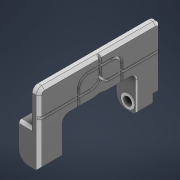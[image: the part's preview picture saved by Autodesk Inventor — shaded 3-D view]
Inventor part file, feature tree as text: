
AUTODESK INVENTOR PART (.ipt)
format: ipt  version: 2022.1 (Build 261234020, 234B)  size: 624,128 bytes
history: native  units: mm
features: move_body x11, direct_edit x9, extrude x9, sketch x9, fillet x7, delete_face x6, chamfer x6, projected_geometry x6, other x3
ambient origin geometry x8: Origin, YZ Plane, XZ Plane, XY Plane, X Axis, Y Axis, Z Axis, Center Point
bodies: Volumenkörper1 (feature_tree)
feature tree (66):
  other  "Bauteil225.ipt"
  direct_edit  "Direktbearbeitung1"
  delete_face  "Fläche löschen1"
  delete_face  "Fläche löschen2"
  direct_edit  "Direktbearbeitung2"
  delete_face  "Fläche löschen3"
  delete_face  "Fläche löschen4"
  direct_edit  "Direktbearbeitung3"
  direct_edit  "Direktbearbeitung4"
  extrude  "Extrusion1"  TaperAngle=0.0deg  [1 undecoded]
  fillet  "Rundung2"  Radius=5.6mm
  delete_face  "Fläche löschen5"
  fillet  "Rundung3"  Radius=6.4mm
  fillet  "Rundung5"  Radius=10.0mm
  chamfer  "Fase1"  Distance=2.0mm Angle=45.0deg
  chamfer  "Fase2"  Distance=2.0mm Angle=45.0deg
  chamfer  "Fase3"  Distance=1.0mm Angle=45.0deg
  extrude  "Extrusion2"  Depth=2.2mm
  fillet  "Rundung6"  Radius=0.81mm
  fillet  "Rundung7"  Radius=2.0mm
  chamfer  "Fase4"  Distance=0.4mm
  fillet  "Rundung8"  Radius=1.0mm
  chamfer  "Fase5"  Distance=0.2mm
  extrude  "Extrusion3"  Depth=0.6mm TaperAngle=45.0deg
  extrude  "Extrusion4"  TaperAngle=90.0deg  [1 undecoded]
  extrude  "Extrusion5"  TaperAngle=90.0deg  [1 undecoded]
  delete_face  "Fläche löschen6"
  direct_edit  "Direktbearbeitung5"
  direct_edit  "Direktbearbeitung6"
  chamfer  "Fase6"  Distance=0.81mm
  extrude  "Extrusion6"  Depth=0.8mm
  extrude  "Extrusion7"  Depth=0.8mm
  direct_edit  "Direktbearbeitung7"
  direct_edit  "Direktbearbeitung8"
  extrude  "Extrusion8"  Depth=0.8mm
  direct_edit  "Direktbearbeitung9"
  extrude  "Extrusion9"  Depth=0.8mm
  fillet  "Rundung9"  Radius=0.8mm
  other  "Volumenkörper1::Bauteil225.ipt"
  other  "Bezeichnung1"
  sketch  "Skizze1"  dims[d0=10.0mm d1=0.0mm d2=0.0mm d3=-0.2mm]
  projected_geometry  "Projizierte Kontur1"
  sketch  "Skizze2"  dims[d4=0.0mm d5=0.0mm d6=-2.0mm]
  projected_geometry  "Projizierte Kontur2"
  sketch  "Skizze3"  dims[d7=0.0mm d8=0.0mm d9=-2.0mm]
  projected_geometry  "Projizierte Kontur3"
  sketch  "Skizze4"  dims[d10=0.0mm d11=0.0mm d12=2.0mm]
  projected_geometry  "Projizierte Kontur4"
  sketch  "Skizze5"  dims[d13=0.0mm d14=0.0mm d15=2.0mm]
  sketch  "Skizze6"  dims[d16=0.0mm d17=0.0mm d18=-3.2mm d19=5.6mm d20=6.4mm d21=10.0mm d22=0.0mm]
  sketch  "Skizze7"  dims[d24=0.3mm]
  projected_geometry  "Projizierte Kontur5"
  sketch  "Skizze8"  dims[d25=3.5mm]
  sketch  "Skizze9"  dims[d27=1.0mm d28=0.4mm d29=2.0mm d30=45.0deg d31=0.4mm d32=2.0mm d33=45.0deg d34=1.0mm d35=2.0mm d36=45.0deg d37=2.2mm d38=0.81mm d39=0.0mm d40=2.0mm d41=0.4mm d42=1.0mm d43=2.0mm d44=45.0deg d45=0.2mm d46=1.2mm d47=0.6mm d48=45.0deg d49=90.0deg d50=90.0deg d51=0.81mm d52=0.0mm d62=22.4mm d63=22.4mm d64=2.955mm d65=0.8mm d66=0.8mm d67=0.8mm d68=0.8mm d69=0.8mm d70=0.8mm d71=0.8mm d72=0.8mm d75=5.0mm d76=2.955mm d78=7.0mm d79=7.0mm d80=3.0mm d81=3.8mm d82=0.8mm d83=0.0mm d84=2.75mm d85=0.8mm d86=0.0mm d87=0.0mm d88=0.0mm d89=0.2mm d90=0.0mm d91=0.0mm d92=0.2mm d93=0.4mm d94=0.6mm d95=45.0deg d96=5.0mm d97=0.2mm d98=0.0mm d99=5.0mm d100=0.2mm d101=0.0mm d102=0.0mm d103=0.0mm d104=-0.2mm d105=0.0mm d106=0.0mm d107=0.8mm d108=10.0mm d109=0.0mm d110=0.0mm d111=0.0mm d112=0.8mm d113=10.0mm d114=0.0mm d115=0.8mm d23=0.5mm]
  projected_geometry  "Projizierte Kontur6"
  move_body  "Verschieben1"
  move_body  "Verschieben2"
  move_body  "Verschieben3"
  move_body  "Verschieben4"
  move_body  "Verschieben5"
  move_body  "Verschieben6"
  move_body  "Verschieben7"
  move_body  "Verschieben8"
  move_body  "Verschieben9"
  move_body  "Verschieben10"
  move_body  "Verschieben11"
note: 3 required parameter values undecoded (feature->parameter linkage not recoverable at this tier; creation-order binding heuristic only, values carry confidence <= 0.55)
